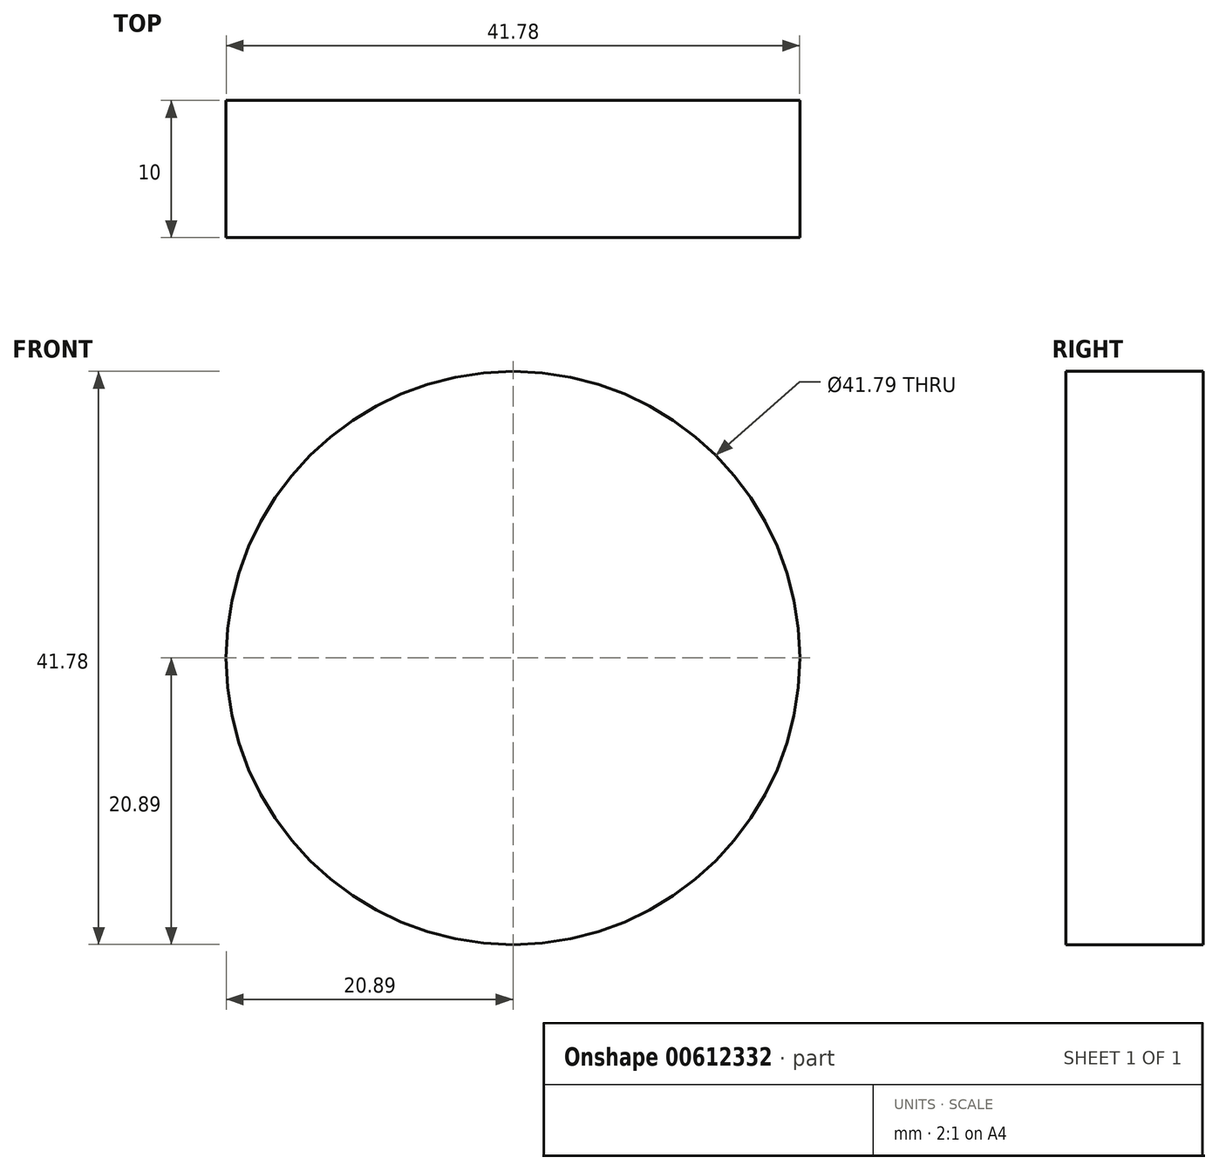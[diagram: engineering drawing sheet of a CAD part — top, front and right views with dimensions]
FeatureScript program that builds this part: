
annotation { "Feature Type Name" : "Feature", "Feature Type Description" : "" }
export const myFeature = defineFeature(function(context is Context, id is Id, definition is map)
    precondition{}
    {
        {
            var Q0;
            Q0=qCreatedBy(makeId("Front.planeOp"),FACE);
            var sketch = newSketch(context, id + "F0", { "sketchPlane" : qUnion([Q0])});
            skCircle(sketch, "E0", {"center": v(0, 0) * mm, "radius": 20.9 * mm});
            skSolve(sketch);
        }
        {
            var Q0;
            Q0 = qSketchRegion(id + "F0", true);
            var sketch = newSketch(context, id + "F1", { "sketchPlane" : qUnion([Q0])});
            skSolve(sketch);
        }
        {
            var Q0;
            Q0 = qSketchRegion(id + "F1", true);
            var Q1;
            Q1=makeQuery(id+"F1.imprint","IMPRINT",FACE,{"disambiguationData":[TD([[makeQuery(id+"F1.imprint","IMPRINT",EDGE,{"derivedFrom":makeQuery(id+"F0.imprint","IMPRINT",EDGE,{"derivedFrom":sQuery(id+"F0.wireOp",EDGE,"E0")})}),1.0]])]});
            var Q2;
            Q2=sQuery(id+"F0.wireOp",EDGE,"E0");
            extrude(context, id + "F2", {"entities" : qUnion([Q0, Q1]), "bodyType" : ToolBodyType.SURFACE, "surfaceEntities" : qUnion([Q2]), "oppositeDirection" : true, "depth" : 10 * mm, "offsetDistance" : 25 * mm});
        }
    });
